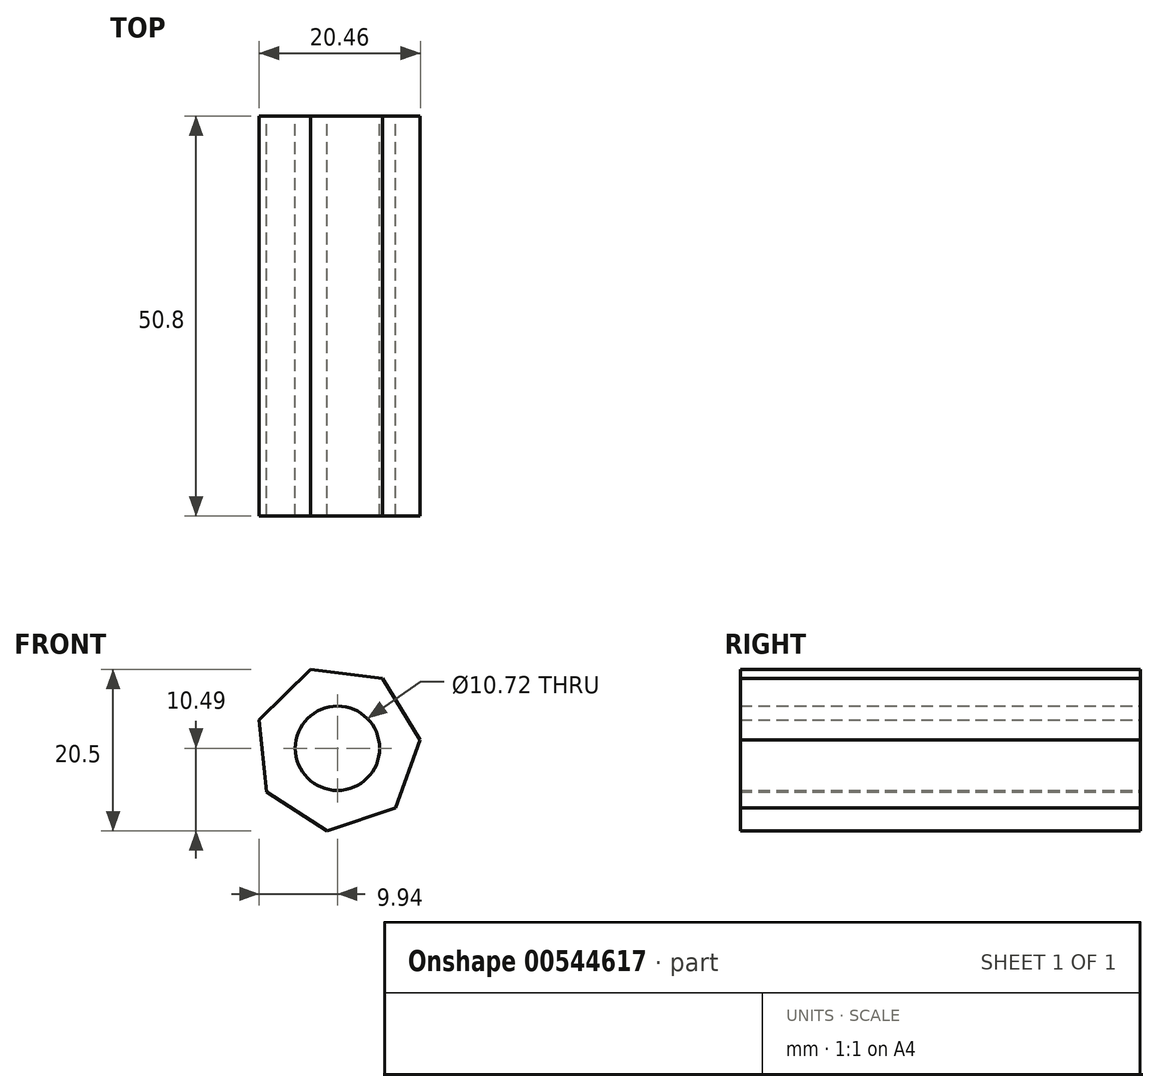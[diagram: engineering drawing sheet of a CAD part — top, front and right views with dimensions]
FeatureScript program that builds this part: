
annotation { "Feature Type Name" : "Feature", "Feature Type Description" : "" }
export const myFeature = defineFeature(function(context is Context, id is Id, definition is map)
    precondition{}
    {
        {
            var Q0;
            Q0=qCreatedBy(makeId("Front.planeOp"),FACE);
            var sketch = newSketch(context, id + "F0", { "sketchPlane" : qUnion([Q0])});
            skCircle(sketch, "E0.cCircle", {"center": v(0, 0) * mm, "radius": 9.53 * mm, "construction": true});
            skLineSegment(sketch, "E0.0", {"start": v(-3.4, 10.01) * mm, "end": v(5.71, 8.9) * mm});
            skLineSegment(sketch, "E0.1", {"start": v(5.71, 8.9) * mm, "end": v(10.52, 1.08) * mm});
            skLineSegment(sketch, "E0.2", {"start": v(10.52, 1.08) * mm, "end": v(7.4, -7.55) * mm});
            skLineSegment(sketch, "E0.3", {"start": v(7.4, -7.55) * mm, "end": v(-1.29, -10.5) * mm});
            skLineSegment(sketch, "E0.4", {"start": v(-1.29, -10.5) * mm, "end": v(-9, -5.53) * mm});
            skLineSegment(sketch, "E0.5", {"start": v(-9, -5.53) * mm, "end": v(-9.94, 3.6) * mm});
            skLineSegment(sketch, "E0.6", {"start": v(-9.94, 3.6) * mm, "end": v(-3.4, 10.01) * mm});
            skPoint(sketch, "E0.0.midPoint", {"position": v(1.16, 9.45) * mm});
            skSolve(sketch);
        }
        {
            var Q0;
            Q0=makeQuery(id+"F0.imprint","IMPRINT",FACE,{"disambiguationData":[TD([[makeQuery(id+"F0.imprint","IMPRINT",EDGE,{"derivedFrom":sQuery(id+"F0.wireOp",EDGE,"E0.0")}),-1.0]])]});
            extrude(context, id + "F1", {"entities" : qUnion([Q0]), "depth" : 50.8 * mm, "offsetDistance" : 25.4 * mm});
        }
        {
            var Q0;
            Q0=makeQuery(id+"F1.opExtrude","CAP_FACE",FACE,{"disambiguationData":[OSD([sQuery(id+"F0.wireOp",EDGE,"E0.0"),sQuery(id+"F0.wireOp",EDGE,"E0.1"),sQuery(id+"F0.wireOp",EDGE,"E0.2"),sQuery(id+"F0.wireOp",EDGE,"E0.3"),sQuery(id+"F0.wireOp",EDGE,"E0.4"),sQuery(id+"F0.wireOp",EDGE,"E0.5"),sQuery(id+"F0.wireOp",EDGE,"E0.6")])],"isStart":true});
            var sketch = newSketch(context, id + "F2", { "sketchPlane" : qUnion([Q0])});
            skPoint(sketch, "E1", {"position": v(0, 0) * mm});
            skSolve(sketch);
        }
        {
            var Q0;
            Q0=sQuery(id+"F2.wireOp",VERTEX,"E1");
            var Q1;
            Q1=makeQuery(id+"F1.opExtrude","SWEPT_BODY",BODY,{"disambiguationData":[OSD([sQuery(id+"F0.wireOp",EDGE,"E0.0"),sQuery(id+"F0.wireOp",EDGE,"E0.1"),sQuery(id+"F0.wireOp",EDGE,"E0.2"),sQuery(id+"F0.wireOp",EDGE,"E0.3"),sQuery(id+"F0.wireOp",EDGE,"E0.4"),sQuery(id+"F0.wireOp",EDGE,"E0.5"),sQuery(id+"F0.wireOp",EDGE,"E0.6")])]});
            hole(context, id + "F3", {"style" : HoleStyle.SIMPLE, "endStyle" : HoleEndStyle.THROUGH, "standardTappedOrClearance" : lookupTablePath({ "fit" : "Normal (ASME)", "standard" : "ANSI", "engagement" : "75%", "pitch" : "13 tpi", "size" : "1/2", "type" : "Tapped" }), "standardBlindInLast" : lookupTablePath({ "fit" : "Free", "standard" : "ANSI", "engagement" : "75%", "pitch" : "13 tpi", "size" : "1/2", "type" : "Tapped" }), "holeDiameter" : 10.72 * mm, "majorDiameter" : 12.7 * mm, "showTappedDepth" : true, "isTappedThrough" : true, "tappedDepth" : 12.7 * mm, "tapClearance" : 3, "locations" : qUnion([Q0]), "scope" : qUnion([Q1])});
        }
    });
